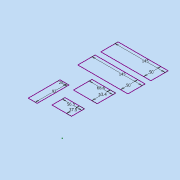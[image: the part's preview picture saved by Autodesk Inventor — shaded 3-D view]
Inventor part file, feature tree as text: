
AUTODESK INVENTOR PART (.ipt)
format: ipt  version: 2017 (Build 210142000, 142)  size: 75,776 bytes
history: native  units: in
note: dims shown in document units (in); Inventor stores cm internally (conversion verified against a paired STEP export)
features: sketch x1
ambient origin geometry x8: Origin, YZ Plane, XZ Plane, XY Plane, X Axis, Y Axis, Z Axis, Center Point
feature tree (1):
  sketch  "Sketch1"  dims[d0=2.2244in d1=1.4764in d2=2.7008in d3=2.1024in d4=3.622in d5=1.0236in d6=5.7087in d7=1.9685in d8=5.7087in d9=1.9685in]
